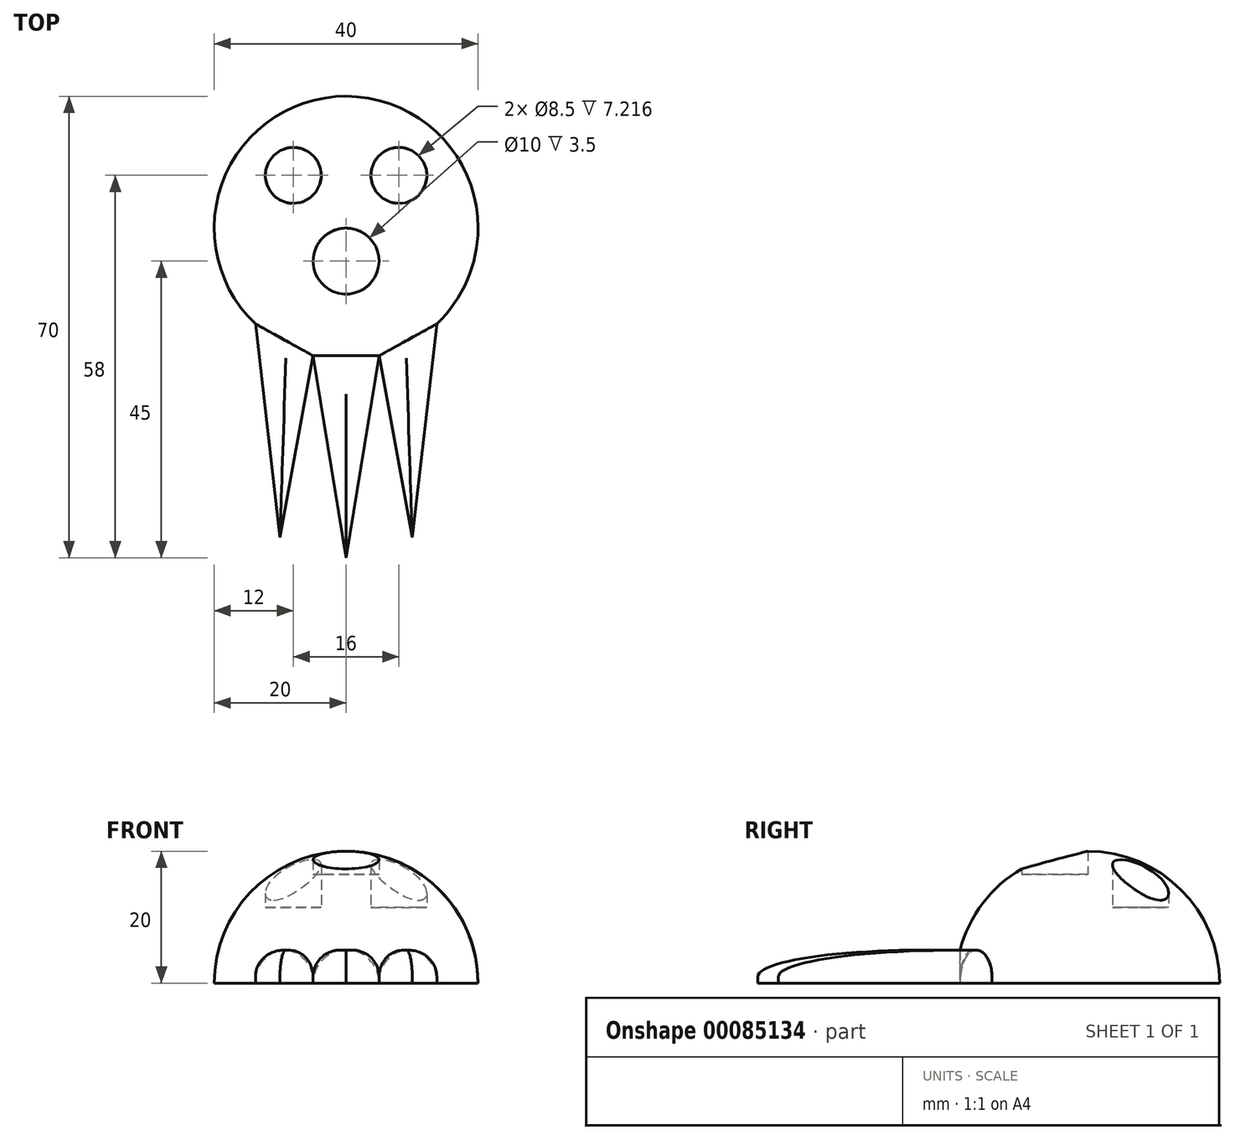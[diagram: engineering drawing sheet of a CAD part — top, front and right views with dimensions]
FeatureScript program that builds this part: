
annotation { "Feature Type Name" : "Feature", "Feature Type Description" : "" }
export const myFeature = defineFeature(function(context is Context, id is Id, definition is map)
    precondition{}
    {
        {
            var Q0;
            Q0=qCreatedBy(makeId("Top.planeOp"),FACE);
            var sketch = newSketch(context, id + "F0", { "sketchPlane" : qUnion([Q0])});
            skCircle(sketch, "E0", {"center": v(0, 0) * mm, "radius": 20 * mm});
            skLineSegment(sketch, "E1", {"start": v(0, 0) * mm, "end": v(0, -50) * mm});
            skLineSegment(sketch, "E2", {"start": v(0, -50) * mm, "end": v(5, -19.36) * mm});
            skLineSegment(sketch, "E3", {"start": v(5, -19.36) * mm, "end": v(-5, -19.36) * mm});
            skLineSegment(sketch, "E4", {"start": v(-5, -19.36) * mm, "end": v(0, -50) * mm});
            skLineSegment(sketch, "E5", {"start": v(-5, -19.36) * mm, "end": v(-10.03, -46.91) * mm});
            skLineSegment(sketch, "E6", {"start": v(-10.03, -46.91) * mm, "end": v(-13.75, -14.52) * mm});
            skLineSegment(sketch, "E7", {"start": v(-13.75, -14.52) * mm, "end": v(-5, -19.36) * mm});
            skLineSegment(sketch, "E8", {"start": v(5, -19.36) * mm, "end": v(13.75, -14.52) * mm});
            skLineSegment(sketch, "E9", {"start": v(13.75, -14.52) * mm, "end": v(10.03, -46.91) * mm});
            skLineSegment(sketch, "E10", {"start": v(10.03, -46.91) * mm, "end": v(5, -19.36) * mm});
            skCircle(sketch, "E11", {"center": v(0, -5) * mm, "radius": 5 * mm});
            skLineSegment(sketch, "E12", {"start": v(0, 0) * mm, "end": v(0, 8) * mm});
            skLineSegment(sketch, "E13", {"start": v(0, 8) * mm, "end": v(8, 8) * mm});
            skLineSegment(sketch, "E14", {"start": v(8, 8) * mm, "end": v(0, 8) * mm});
            skLineSegment(sketch, "E15", {"start": v(0, 8) * mm, "end": v(-8, 8) * mm});
            skCircle(sketch, "E16", {"center": v(8, 8) * mm, "radius": 4.25 * mm});
            skCircle(sketch, "E17", {"center": v(-8, 8) * mm, "radius": 4.25 * mm});
            skSolve(sketch);
        }
        {
            var Q0;
            {var subQ1=sQuery(id+"F0.wireOp",EDGE,"E5");Q0=makeQuery(id+"F0.imprint","IMPRINT",FACE,{"disambiguationData":[TD([[makeQuery(id+"F0.imprint","IMPRINT",EDGE,{"derivedFrom":subQ1}),-1.0]])]});}
            var Q1;
            {var subQ0=sQuery(id+"F0.wireOp",EDGE,"E4");Q1=makeQuery(id+"F0.imprint","IMPRINT",FACE,{"disambiguationData":[TD([[makeQuery(id+"F0.imprint","IMPRINT",EDGE,{"derivedFrom":subQ0}),1.0]])]});}
            var Q2;
            {var subQ0=sQuery(id+"F0.wireOp",EDGE,"E2");Q2=makeQuery(id+"F0.imprint","IMPRINT",FACE,{"disambiguationData":[TD([[makeQuery(id+"F0.imprint","IMPRINT",EDGE,{"derivedFrom":subQ0}),1.0]])]});}
            var Q3;
            {var subQ3=sQuery(id+"F0.wireOp",EDGE,"E9");Q3=makeQuery(id+"F0.imprint","IMPRINT",FACE,{"disambiguationData":[TD([[makeQuery(id+"F0.imprint","IMPRINT",EDGE,{"derivedFrom":subQ3}),-1.0]])]});}
            var Q4;
            {var subQ0=sQuery(id+"F0.wireOp",EDGE,"E3");var subQ3=sQuery(id+"F0.wireOp",EDGE,"E1");var subQ5=makeQuery(id+"F0.imprint","INTERSECT",VERTEX,{"derivedFrom":[subQ3,subQ0]});Q4=makeQuery(id+"F0.imprint","IMPRINT",FACE,{"disambiguationData":[TD([[makeQuery(id+"F0.imprint","IMPRINT",EDGE,{"disambiguationData":[TD([[subQ5,-1.0]])],"derivedFrom":subQ3}),-1.0]])]});}
            var Q5;
            {var subQ0=sQuery(id+"F0.wireOp",EDGE,"E3");var subQ3=sQuery(id+"F0.wireOp",EDGE,"E1");var subQ5=makeQuery(id+"F0.imprint","INTERSECT",VERTEX,{"derivedFrom":[subQ3,subQ0]});Q5=makeQuery(id+"F0.imprint","IMPRINT",FACE,{"disambiguationData":[TD([[makeQuery(id+"F0.imprint","IMPRINT",EDGE,{"disambiguationData":[TD([[subQ5,-1.0]])],"derivedFrom":subQ3}),1.0]])]});}
            var Q6;
            {var subQ0=sQuery(id+"F0.wireOp",EDGE,"E8");Q6=makeQuery(id+"F0.imprint","IMPRINT",FACE,{"disambiguationData":[TD([[makeQuery(id+"F0.imprint","IMPRINT",EDGE,{"derivedFrom":subQ0}),-1.0]])]});}
            var Q7;
            {var subQ0=sQuery(id+"F0.wireOp",EDGE,"E7");Q7=makeQuery(id+"F0.imprint","IMPRINT",FACE,{"disambiguationData":[TD([[makeQuery(id+"F0.imprint","IMPRINT",EDGE,{"derivedFrom":subQ0}),-1.0]])]});}
            extrude(context, id + "F1", {"entities" : qUnion([Q0, Q1, Q2, Q3, Q4, Q5, Q6, Q7]), "depth" : 5 * mm});
        }
        {
            var Q0;
            Q0=makeQuery(id+"F0.imprint","IMPRINT",FACE,{"disambiguationData":[TD([[makeQuery(id+"F0.imprint","IMPRINT",EDGE,{"derivedFrom":sQuery(id+"F0.wireOp",EDGE,"E17")}),1.0]])]});
            var Q1;
            {var subQ0=sQuery(id+"F0.wireOp",EDGE,"E11");var subQ1=sQuery(id+"F0.wireOp",EDGE,"E1");var subQ2=makeQuery(id+"F0.imprint","INTERSECT",VERTEX,{"disambiguationData":[OD(0.0)],"derivedFrom":[subQ1,subQ0]});Q1=makeQuery(id+"F0.imprint","IMPRINT",FACE,{"disambiguationData":[TD([[makeQuery(id+"F0.imprint","IMPRINT",EDGE,{"disambiguationData":[TD([[subQ2,-1.0]])],"derivedFrom":subQ1}),1.0]])]});}
            var Q2;
            {var subQ0=sQuery(id+"F0.wireOp",EDGE,"E11");var subQ1=sQuery(id+"F0.wireOp",EDGE,"E1");var subQ2=makeQuery(id+"F0.imprint","INTERSECT",VERTEX,{"disambiguationData":[OD(0.0)],"derivedFrom":[subQ1,subQ0]});Q2=makeQuery(id+"F0.imprint","IMPRINT",FACE,{"disambiguationData":[TD([[makeQuery(id+"F0.imprint","IMPRINT",EDGE,{"disambiguationData":[TD([[subQ2,-1.0]])],"derivedFrom":subQ1}),-1.0]])]});}
            var Q3;
            Q3=makeQuery(id+"F0.imprint","IMPRINT",FACE,{"disambiguationData":[TD([[makeQuery(id+"F0.imprint","IMPRINT",EDGE,{"derivedFrom":sQuery(id+"F0.wireOp",EDGE,"E16")}),1.0]])]});
            var Q4;
            {var subQ0=sQuery(id+"F0.wireOp",EDGE,"E7");Q4=makeQuery(id+"F0.imprint","IMPRINT",FACE,{"disambiguationData":[TD([[makeQuery(id+"F0.imprint","IMPRINT",EDGE,{"derivedFrom":subQ0}),1.0]])]});}
            extrude(context, id + "F2", {"entities" : qUnion([Q0, Q1, Q2, Q3, Q4]), "depth" : 20 * mm});
        }
        {
            var Q0;
            Q0=makeQuery(id+"F2.opExtrude","CAP_EDGE",EDGE,{"disambiguationData":[OSD([sQuery(id+"F0.wireOp",EDGE,"E0")])],"isStart":false});
            fillet(context, id + "F3", {"entities" : qUnion([Q0]), "radius" : 20 * mm, "tangentPropagation" : true, "allowEdgeOverflow" : false});
        }
        {
            var Q0;
            Q0=makeQuery(id+"F1.opExtrude","CAP_EDGE",EDGE,{"disambiguationData":[OSD([sQuery(id+"F0.wireOp",EDGE,"E6")])],"isStart":false});
            var Q1;
            Q1=makeQuery(id+"F1.opExtrude","CAP_EDGE",EDGE,{"disambiguationData":[OSD([sQuery(id+"F0.wireOp",EDGE,"E5")])],"isStart":false});
            fillet(context, id + "F4", {"entities" : qUnion([Q0, Q1]), "radius" : 4 * mm, "tangentPropagation" : true, "allowEdgeOverflow" : false});
        }
        {
            var Q0;
            Q0=makeQuery(id+"F1.opExtrude","CAP_EDGE",EDGE,{"disambiguationData":[OSD([sQuery(id+"F0.wireOp",EDGE,"E4")])],"isStart":false});
            var Q1;
            Q1=makeQuery(id+"F1.opExtrude","CAP_EDGE",EDGE,{"disambiguationData":[OSD([sQuery(id+"F0.wireOp",EDGE,"E2")])],"isStart":false});
            var Q2;
            Q2=makeQuery(id+"F1.opExtrude","CAP_EDGE",EDGE,{"disambiguationData":[OSD([sQuery(id+"F0.wireOp",EDGE,"E10")])],"isStart":false});
            var Q3;
            Q3=makeQuery(id+"F1.opExtrude","CAP_EDGE",EDGE,{"disambiguationData":[OSD([sQuery(id+"F0.wireOp",EDGE,"E9")])],"isStart":false});
            fillet(context, id + "F5", {"entities" : qUnion([Q0, Q1, Q2, Q3]), "radius" : 4 * mm, "tangentPropagation" : true, "allowEdgeOverflow" : false});
        }
        {
            var Q0;
            Q0=sQuery(id+"F0.wireOp",VERTEX,"E13.end");
            var Q1;
            Q1=sQuery(id+"F0.wireOp",VERTEX,"E15.end");
            var Q2;
            Q2=makeQuery(id+"F2.opExtrude","SWEPT_BODY",BODY,{"disambiguationData":[OSD([sQuery(id+"F0.wireOp",EDGE,"E0"),sQuery(id+"F0.wireOp",EDGE,"E3"),sQuery(id+"F0.wireOp",EDGE,"E7"),sQuery(id+"F0.wireOp",EDGE,"E8")])]});
            hole(context, id + "F6", {"style" : HoleStyle.SIMPLE, "endStyle" : HoleEndStyle.THROUGH, "oppositeDirection" : true, "holeDiameter" : 8.5 * mm, "locations" : qUnion([Q0, Q1]), "scope" : qUnion([Q2]), "isTappedThrough" : true});
        }
        {
            var Q0;
            Q0=sQuery(id+"F0.wireOp",VERTEX,"E11.center");
            var Q1;
            Q1=makeQuery(id+"F2.opExtrude","SWEPT_BODY",BODY,{"disambiguationData":[OSD([sQuery(id+"F0.wireOp",EDGE,"E0"),sQuery(id+"F0.wireOp",EDGE,"E3"),sQuery(id+"F0.wireOp",EDGE,"E7"),sQuery(id+"F0.wireOp",EDGE,"E8")])]});
            hole(context, id + "F7", {"style" : HoleStyle.SIMPLE, "endStyle" : HoleEndStyle.THROUGH, "oppositeDirection" : true, "holeDiameter" : 10 * mm, "locations" : qUnion([Q0]), "scope" : qUnion([Q1]), "isTappedThrough" : true});
        }
        {
            var Q0;
            Q0=makeQuery(id+"F0.imprint","IMPRINT",FACE,{"disambiguationData":[TD([[makeQuery(id+"F0.imprint","IMPRINT",EDGE,{"derivedFrom":sQuery(id+"F0.wireOp",EDGE,"E17")}),1.0]])]});
            var Q1;
            Q1=makeQuery(id+"F0.imprint","IMPRINT",FACE,{"disambiguationData":[TD([[makeQuery(id+"F0.imprint","IMPRINT",EDGE,{"derivedFrom":sQuery(id+"F0.wireOp",EDGE,"E16")}),1.0]])]});
            var Q2;
            {var subQ0=sQuery(id+"F0.wireOp",EDGE,"E11");var subQ1=sQuery(id+"F0.wireOp",EDGE,"E1");var subQ2=makeQuery(id+"F0.imprint","INTERSECT",VERTEX,{"disambiguationData":[OD(0.0)],"derivedFrom":[subQ1,subQ0]});Q2=makeQuery(id+"F0.imprint","IMPRINT",FACE,{"disambiguationData":[TD([[makeQuery(id+"F0.imprint","IMPRINT",EDGE,{"disambiguationData":[TD([[subQ2,-1.0]])],"derivedFrom":subQ1}),1.0]])]});}
            var Q3;
            {var subQ0=sQuery(id+"F0.wireOp",EDGE,"E11");var subQ1=sQuery(id+"F0.wireOp",EDGE,"E1");var subQ2=makeQuery(id+"F0.imprint","INTERSECT",VERTEX,{"disambiguationData":[OD(0.0)],"derivedFrom":[subQ1,subQ0]});Q3=makeQuery(id+"F0.imprint","IMPRINT",FACE,{"disambiguationData":[TD([[makeQuery(id+"F0.imprint","IMPRINT",EDGE,{"disambiguationData":[TD([[subQ2,-1.0]])],"derivedFrom":subQ1}),-1.0]])]});}
            extrude(context, id + "F8", {"entities" : qUnion([Q0, Q1, Q2, Q3]), "operationType" : NewBodyOperationType.ADD, "depth" : 11.5 * mm});
        }
        {
            var Q0;
            Q0=makeQuery(id+"F8.opExtrude","CAP_FACE",FACE,{"disambiguationData":[OSD([sQuery(id+"F0.wireOp",EDGE,"E11")])],"isStart":false});
            extrude(context, id + "F9", {"entities" : qUnion([Q0]), "operationType" : NewBodyOperationType.ADD, "depth" : 5 * mm});
        }
    });
